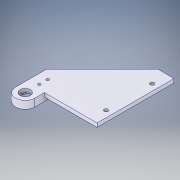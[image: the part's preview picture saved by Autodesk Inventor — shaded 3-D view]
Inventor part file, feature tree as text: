
AUTODESK INVENTOR PART (.ipt)
format: ipt  version: 2017 (Build 210142000, 142)  size: 162,816 bytes
history: native  units: in
note: dims shown in document units (in); Inventor stores cm internally (conversion verified against a paired STEP export)
features: extrude x2, sketch x2, projected_geometry x1
ambient origin geometry x8: Origin, YZ Plane, XZ Plane, XY Plane, X Axis, Y Axis, Z Axis, Center Point
bodies: Solid1 (feature_tree)
feature tree (5):
  extrude  "Extrusion1"  TaperAngle=90.0deg  [1 undecoded]
  extrude  "Extrusion3"  Depth=1.6142in
  sketch  "Sketch3"  dims[d6=2.3622in d7=90.0deg]
  sketch  "Sketch6"  dims[d8=0.4929in d9=1.6142in d10=0.2953in d11=0.5906in d13=0.9456in d14=0.1181in d15=0.0in d18=0.1969in d19=0.4724in d20=0.4724in d21=0.1181in d22=0.1181in d25=0.315in d26=0.4335in d27=0.2562in d28=0.0787in d29=0.0787in d31=0.4331in d32=0.0591in d33=0.2362in d34=0.1181in d35=0.2362in d36=0.0in]
  projected_geometry  "Projected Loop3"
note: 1 required parameter value undecoded (feature->parameter linkage not recoverable at this tier; creation-order binding heuristic only, values carry confidence <= 0.55)
